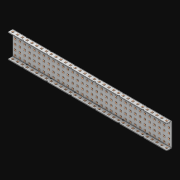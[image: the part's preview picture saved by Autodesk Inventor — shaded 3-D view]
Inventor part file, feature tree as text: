
AUTODESK INVENTOR PART (.ipt)
format: ipt  version: 2021 (Build 250183000, 183)  size: 3,894,272 bytes
history: native  units: in
note: dims shown in document units (in); Inventor stores cm internally (conversion verified against a paired STEP export)
features: extrude x232, other x231, sketch x4, thicken_offset x3, pattern_linear x3, imported_body x1
ambient origin geometry x8: Origin, YZ Plane, XZ Plane, XY Plane, X Axis, Y Axis, Z Axis, Center Point
bodies: Solid1 (feature_tree)
feature tree (474):
  thicken_offset  "Thicken1"
  thicken_offset  "Thicken2"
  thicken_offset  "Thicken3"
  pattern_linear  "Rectangular Pattern1"  Spacing1=0.001in  [1 undecoded]
  pattern_linear  "Rectangular Pattern2"  Spacing1=0.001in  [1 undecoded]
  pattern_linear  "Rectangular Pattern3"  Spacing1=0.182in  [1 undecoded]
  extrude  "Extrusion1"  Depth=0.063in TaperAngle=0.0deg
  sketch  "Sketch1"  dims[d0=0.001in]
  other  "Srf1"
  sketch  "Sketch2"  dims[d1=0.001in]
  other  "Srf2"
  sketch  "Sketch3"  dims[d2=0.001in]
  other  "Srf3"
  other  "Srf4"
  other  "Srf5"
  other  "Srf6"
  other  "Srf7"
  other  "Srf8"
  other  "Srf9"
  other  "Srf10"
  other  "Srf11"
  other  "Srf12"
  other  "Srf13"
  other  "Srf14"
  other  "Srf15"
  other  "Srf16"
  other  "Srf17"
  other  "Srf18"
  other  "Srf19"
  other  "Srf20"
  other  "Srf21"
  other  "Srf22"
  other  "Srf23"
  other  "Srf24"
  other  "Srf25"
  other  "Srf26"
  other  "Srf27"
  other  "Srf28"
  other  "Srf29"
  other  "Srf30"
  other  "Srf31"
  other  "Srf32"
  other  "Srf33"
  other  "Srf34"
  other  "Srf38"
  other  "Srf39"
  other  "Srf40"
  other  "Srf41"
  other  "Srf42"
  other  "Srf43"
  other  "Srf44"
  other  "Srf45"
  other  "Srf46"
  other  "Srf47"
  other  "Srf48"
  other  "Srf49"
  other  "Srf50"
  other  "Srf51"
  other  "Srf52"
  other  "Srf53"
  other  "Srf54"
  other  "Srf55"
  other  "Srf56"
  other  "Srf57"
  other  "Srf58"
  other  "Srf59"
  other  "Srf60"
  other  "Srf61"
  other  "Srf62"
  other  "Srf63"
  other  "Srf64"
  other  "Srf65"
  other  "Srf66"
  other  "Srf67"
  other  "Srf68"
  other  "Srf72"
  other  "Srf73"
  other  "Srf74"
  other  "Srf75"
  other  "Srf76"
  other  "Srf77"
  other  "Srf78"
  other  "Srf79"
  other  "Srf80"
  other  "Srf81"
  other  "Srf82"
  other  "Srf83"
  other  "Srf84"
  other  "Srf85"
  other  "Srf86"
  other  "Srf87"
  other  "Srf88"
  other  "Srf89"
  other  "Srf90"
  other  "Srf91"
  other  "Srf92"
  other  "Srf93"
  other  "Srf94"
  other  "Srf95"
  other  "Srf96"
  other  "Srf97"
  other  "Srf98"
  other  "Srf99"
  other  "Srf100"
  other  "Srf101"
  other  "Srf102"
  other  "Srf106"
  other  "Srf107"
  other  "Srf108"
  other  "Srf109"
  other  "Srf110"
  other  "Srf111"
  other  "Srf112"
  other  "Srf113"
  other  "Srf114"
  other  "Srf115"
  other  "Srf116"
  other  "Srf117"
  other  "Srf118"
  other  "Srf119"
  other  "Srf120"
  other  "Srf121"
  other  "Srf122"
  other  "Srf123"
  other  "Srf124"
  other  "Srf125"
  other  "Srf126"
  other  "Srf127"
  other  "Srf128"
  other  "Srf129"
  other  "Srf130"
  other  "Srf131"
  other  "Srf132"
  other  "Srf133"
  other  "Srf134"
  other  "Srf135"
  other  "Srf136"
  other  "Srf137"
  other  "Srf141"
  other  "Srf142"
  other  "Srf143"
  other  "Srf144"
  other  "Srf145"
  other  "Srf146"
  other  "Srf147"
  other  "Srf148"
  other  "Srf149"
  other  "Srf150"
  other  "Srf151"
  other  "Srf152"
  other  "Srf153"
  other  "Srf154"
  other  "Srf155"
  other  "Srf156"
  other  "Srf157"
  other  "Srf158"
  other  "Srf159"
  other  "Srf160"
  other  "Srf161"
  other  "Srf162"
  other  "Srf163"
  other  "Srf164"
  other  "Srf165"
  other  "Srf166"
  other  "Srf167"
  other  "Srf168"
  other  "Srf169"
  other  "Srf170"
  other  "Srf171"
  other  "Srf172"
  other  "Srf176"
  other  "Srf177"
  other  "Srf178"
  other  "Srf179"
  other  "Srf180"
  other  "Srf181"
  other  "Srf182"
  other  "Srf183"
  other  "Srf184"
  other  "Srf185"
  other  "Srf186"
  other  "Srf187"
  other  "Srf188"
  other  "Srf189"
  other  "Srf190"
  other  "Srf191"
  other  "Srf192"
  other  "Srf193"
  other  "Srf194"
  other  "Srf195"
  other  "Srf196"
  other  "Srf197"
  other  "Srf198"
  other  "Srf199"
  other  "Srf200"
  other  "Srf201"
  other  "Srf202"
  other  "Srf203"
  other  "Srf204"
  other  "Srf205"
  other  "Srf206"
  other  "Srf207"
  other  "Srf211"
  other  "Srf212"
  other  "Srf213"
  other  "Srf214"
  other  "Srf215"
  other  "Srf216"
  other  "Srf217"
  other  "Srf218"
  other  "Srf219"
  other  "Srf220"
  other  "Srf221"
  other  "Srf222"
  other  "Srf223"
  other  "Srf224"
  other  "Srf225"
  other  "Srf226"
  other  "Srf227"
  other  "Srf228"
  other  "Srf229"
  other  "Srf230"
  other  "Srf231"
  other  "Srf232"
  other  "Srf233"
  other  "Srf234"
  other  "Srf235"
  other  "Srf236"
  other  "Srf237"
  other  "Srf238"
  other  "Srf239"
  other  "Srf240"
  other  "Srf241"
  other  "Srf242"
  sketch  "Sketch4"  dims[d3=0.001in d4=0.001in d5=0.001in d6=0.182in d7=0.063in d8=0.0in d9=0.182in d10=0.063in d11=0.0in d12=0.182in d13=0.063in d14=0.0in d17=0.5in d18=12.9921in d20=0.5in d21=12.9921in d23=0.5in d24=1.9685in d26=0.5in d27=1.0in d28=0.0in]
  other  "Srf246"
  other  "Srf247"
  other  "Srf248"
  other  "Srf249"
  other  "Srf250"
  other  "Srf251"
  other  "Srf252"
  imported_body  "Imported1"
  extrude  "ExtrusionSrf1"  Depth=1.0in
  extrude  "ExtrusionSrf2"  Depth=0.063in TaperAngle=0.0deg
  extrude  "ExtrusionSrf3"  Depth=1.0in
  extrude  "ExtrusionSrf4"  Depth=0.063in TaperAngle=0.0deg
  extrude  "ExtrusionSrf5"  Depth=0.5in
  extrude  "ExtrusionSrf6"  Depth=1.0in
  extrude  "ExtrusionSrf7"  Depth=0.5in
  extrude  "ExtrusionSrf8"  Depth=1.0in
  extrude  "ExtrusionSrf9"  Depth=0.5in
  extrude  "ExtrusionSrf10"  Depth=0.5in
  extrude  "ExtrusionSrf11"  Depth=1.0in
  extrude  "ExtrusionSrf12"  TaperAngle=0.0deg  [1 undecoded]
  extrude  "ExtrusionSrf13"  [1 undecoded]
  extrude  "ExtrusionSrf14"  [1 undecoded]
  extrude  "ExtrusionSrf15"  [1 undecoded]
  extrude  "ExtrusionSrf16"  [1 undecoded]
  extrude  "ExtrusionSrf17"  [1 undecoded]
  extrude  "ExtrusionSrf18"  [1 undecoded]
  extrude  "ExtrusionSrf19"  [1 undecoded]
  extrude  "ExtrusionSrf20"  [1 undecoded]
  extrude  "ExtrusionSrf21"  [1 undecoded]
  extrude  "ExtrusionSrf22"  [1 undecoded]
  extrude  "ExtrusionSrf23"  [1 undecoded]
  extrude  "ExtrusionSrf24"  [1 undecoded]
  extrude  "ExtrusionSrf25"  [1 undecoded]
  extrude  "ExtrusionSrf26"  [1 undecoded]
  extrude  "ExtrusionSrf27"  [1 undecoded]
  extrude  "ExtrusionSrf28"  [1 undecoded]
  extrude  "ExtrusionSrf29"  [1 undecoded]
  extrude  "ExtrusionSrf30"  [1 undecoded]
  extrude  "ExtrusionSrf31"  [1 undecoded]
  extrude  "ExtrusionSrf32"  [1 undecoded]
  extrude  "ExtrusionSrf33"  [1 undecoded]
  extrude  "ExtrusionSrf34"  [1 undecoded]
  extrude  "ExtrusionSrf38"  [1 undecoded]
  extrude  "ExtrusionSrf39"  [1 undecoded]
  extrude  "ExtrusionSrf40"  [1 undecoded]
  extrude  "ExtrusionSrf41"  [1 undecoded]
  extrude  "ExtrusionSrf42"  [1 undecoded]
  extrude  "ExtrusionSrf43"  [1 undecoded]
  extrude  "ExtrusionSrf44"  [1 undecoded]
  extrude  "ExtrusionSrf45"  [1 undecoded]
  extrude  "ExtrusionSrf46"  [1 undecoded]
  extrude  "ExtrusionSrf47"  [1 undecoded]
  extrude  "ExtrusionSrf48"  [1 undecoded]
  extrude  "ExtrusionSrf49"  [1 undecoded]
  extrude  "ExtrusionSrf50"  [1 undecoded]
  extrude  "ExtrusionSrf51"  [1 undecoded]
  extrude  "ExtrusionSrf52"  [1 undecoded]
  extrude  "ExtrusionSrf53"  [1 undecoded]
  extrude  "ExtrusionSrf54"  [1 undecoded]
  extrude  "ExtrusionSrf55"  [1 undecoded]
  extrude  "ExtrusionSrf56"  [1 undecoded]
  extrude  "ExtrusionSrf57"  [1 undecoded]
  extrude  "ExtrusionSrf58"  [1 undecoded]
  extrude  "ExtrusionSrf59"  [1 undecoded]
  extrude  "ExtrusionSrf60"  [1 undecoded]
  extrude  "ExtrusionSrf61"  [1 undecoded]
  extrude  "ExtrusionSrf62"  [1 undecoded]
  extrude  "ExtrusionSrf63"  [1 undecoded]
  extrude  "ExtrusionSrf64"  [1 undecoded]
  extrude  "ExtrusionSrf65"  [1 undecoded]
  extrude  "ExtrusionSrf66"  [1 undecoded]
  extrude  "ExtrusionSrf67"  [1 undecoded]
  extrude  "ExtrusionSrf68"  [1 undecoded]
  extrude  "ExtrusionSrf72"  [1 undecoded]
  extrude  "ExtrusionSrf73"  [1 undecoded]
  extrude  "ExtrusionSrf74"  [1 undecoded]
  extrude  "ExtrusionSrf75"  [1 undecoded]
  extrude  "ExtrusionSrf76"  [1 undecoded]
  extrude  "ExtrusionSrf77"  [1 undecoded]
  extrude  "ExtrusionSrf78"  [1 undecoded]
  extrude  "ExtrusionSrf79"  [1 undecoded]
  extrude  "ExtrusionSrf80"  [1 undecoded]
  extrude  "ExtrusionSrf81"  [1 undecoded]
  extrude  "ExtrusionSrf82"  [1 undecoded]
  extrude  "ExtrusionSrf83"  [1 undecoded]
  extrude  "ExtrusionSrf84"  [1 undecoded]
  extrude  "ExtrusionSrf85"  [1 undecoded]
  extrude  "ExtrusionSrf86"  [1 undecoded]
  extrude  "ExtrusionSrf87"  [1 undecoded]
  extrude  "ExtrusionSrf88"  [1 undecoded]
  extrude  "ExtrusionSrf89"  [1 undecoded]
  extrude  "ExtrusionSrf90"  [1 undecoded]
  extrude  "ExtrusionSrf91"  [1 undecoded]
  extrude  "ExtrusionSrf92"  [1 undecoded]
  extrude  "ExtrusionSrf93"  [1 undecoded]
  extrude  "ExtrusionSrf94"  [1 undecoded]
  extrude  "ExtrusionSrf95"  [1 undecoded]
  extrude  "ExtrusionSrf96"  [1 undecoded]
  extrude  "ExtrusionSrf97"  [1 undecoded]
  extrude  "ExtrusionSrf98"  [1 undecoded]
  extrude  "ExtrusionSrf99"  [1 undecoded]
  extrude  "ExtrusionSrf100"  [1 undecoded]
  extrude  "ExtrusionSrf101"  [1 undecoded]
  extrude  "ExtrusionSrf102"  [1 undecoded]
  extrude  "ExtrusionSrf106"  [1 undecoded]
  extrude  "ExtrusionSrf107"  [1 undecoded]
  extrude  "ExtrusionSrf108"  [1 undecoded]
  extrude  "ExtrusionSrf109"  [1 undecoded]
  extrude  "ExtrusionSrf110"  [1 undecoded]
  extrude  "ExtrusionSrf111"  [1 undecoded]
  extrude  "ExtrusionSrf112"  [1 undecoded]
  extrude  "ExtrusionSrf113"  [1 undecoded]
  extrude  "ExtrusionSrf114"  [1 undecoded]
  extrude  "ExtrusionSrf115"  [1 undecoded]
  extrude  "ExtrusionSrf116"  [1 undecoded]
  extrude  "ExtrusionSrf117"  [1 undecoded]
  extrude  "ExtrusionSrf118"  [1 undecoded]
  extrude  "ExtrusionSrf119"  [1 undecoded]
  extrude  "ExtrusionSrf120"  [1 undecoded]
  extrude  "ExtrusionSrf121"  [1 undecoded]
  extrude  "ExtrusionSrf122"  [1 undecoded]
  extrude  "ExtrusionSrf123"  [1 undecoded]
  extrude  "ExtrusionSrf124"  [1 undecoded]
  extrude  "ExtrusionSrf125"  [1 undecoded]
  extrude  "ExtrusionSrf126"  [1 undecoded]
  extrude  "ExtrusionSrf127"  [1 undecoded]
  extrude  "ExtrusionSrf128"  [1 undecoded]
  extrude  "ExtrusionSrf129"  [1 undecoded]
  extrude  "ExtrusionSrf130"  [1 undecoded]
  extrude  "ExtrusionSrf131"  [1 undecoded]
  extrude  "ExtrusionSrf132"  [1 undecoded]
  extrude  "ExtrusionSrf133"  [1 undecoded]
  extrude  "ExtrusionSrf134"  [1 undecoded]
  extrude  "ExtrusionSrf135"  [1 undecoded]
  extrude  "ExtrusionSrf136"  [1 undecoded]
  extrude  "ExtrusionSrf137"  [1 undecoded]
  extrude  "ExtrusionSrf141"  [1 undecoded]
  extrude  "ExtrusionSrf142"  [1 undecoded]
  extrude  "ExtrusionSrf143"  [1 undecoded]
  extrude  "ExtrusionSrf144"  [1 undecoded]
  extrude  "ExtrusionSrf145"  [1 undecoded]
  extrude  "ExtrusionSrf146"  [1 undecoded]
  extrude  "ExtrusionSrf147"  [1 undecoded]
  extrude  "ExtrusionSrf148"  [1 undecoded]
  extrude  "ExtrusionSrf149"  [1 undecoded]
  extrude  "ExtrusionSrf150"  [1 undecoded]
  extrude  "ExtrusionSrf151"  [1 undecoded]
  extrude  "ExtrusionSrf152"  [1 undecoded]
  extrude  "ExtrusionSrf153"  [1 undecoded]
  extrude  "ExtrusionSrf154"  [1 undecoded]
  extrude  "ExtrusionSrf155"  [1 undecoded]
  extrude  "ExtrusionSrf156"  [1 undecoded]
  extrude  "ExtrusionSrf157"  [1 undecoded]
  extrude  "ExtrusionSrf158"  [1 undecoded]
  extrude  "ExtrusionSrf159"  [1 undecoded]
  extrude  "ExtrusionSrf160"  [1 undecoded]
  extrude  "ExtrusionSrf161"  [1 undecoded]
  extrude  "ExtrusionSrf162"  [1 undecoded]
  extrude  "ExtrusionSrf163"  [1 undecoded]
  extrude  "ExtrusionSrf164"  [1 undecoded]
  extrude  "ExtrusionSrf165"  [1 undecoded]
  extrude  "ExtrusionSrf166"  [1 undecoded]
  extrude  "ExtrusionSrf167"  [1 undecoded]
  extrude  "ExtrusionSrf168"  [1 undecoded]
  extrude  "ExtrusionSrf169"  [1 undecoded]
  extrude  "ExtrusionSrf170"  [1 undecoded]
  extrude  "ExtrusionSrf171"  [1 undecoded]
  extrude  "ExtrusionSrf172"  [1 undecoded]
  extrude  "ExtrusionSrf176"  [1 undecoded]
  extrude  "ExtrusionSrf177"  [1 undecoded]
  extrude  "ExtrusionSrf178"  [1 undecoded]
  extrude  "ExtrusionSrf179"  [1 undecoded]
  extrude  "ExtrusionSrf180"  [1 undecoded]
  extrude  "ExtrusionSrf181"  [1 undecoded]
  extrude  "ExtrusionSrf182"  [1 undecoded]
  extrude  "ExtrusionSrf183"  [1 undecoded]
  extrude  "ExtrusionSrf184"  [1 undecoded]
  extrude  "ExtrusionSrf185"  [1 undecoded]
  extrude  "ExtrusionSrf186"  [1 undecoded]
  extrude  "ExtrusionSrf187"  [1 undecoded]
  extrude  "ExtrusionSrf188"  [1 undecoded]
  extrude  "ExtrusionSrf189"  [1 undecoded]
  extrude  "ExtrusionSrf190"  [1 undecoded]
  extrude  "ExtrusionSrf191"  [1 undecoded]
  extrude  "ExtrusionSrf192"  [1 undecoded]
  extrude  "ExtrusionSrf193"  [1 undecoded]
  extrude  "ExtrusionSrf194"  [1 undecoded]
  extrude  "ExtrusionSrf195"  [1 undecoded]
  extrude  "ExtrusionSrf196"  [1 undecoded]
  extrude  "ExtrusionSrf197"  [1 undecoded]
  extrude  "ExtrusionSrf198"  [1 undecoded]
  extrude  "ExtrusionSrf199"  [1 undecoded]
  extrude  "ExtrusionSrf200"  [1 undecoded]
  extrude  "ExtrusionSrf201"  [1 undecoded]
  extrude  "ExtrusionSrf202"  [1 undecoded]
  extrude  "ExtrusionSrf203"  [1 undecoded]
  extrude  "ExtrusionSrf204"  [1 undecoded]
  extrude  "ExtrusionSrf205"  [1 undecoded]
  extrude  "ExtrusionSrf206"  [1 undecoded]
  extrude  "ExtrusionSrf207"  [1 undecoded]
  extrude  "ExtrusionSrf211"  [1 undecoded]
  extrude  "ExtrusionSrf212"  [1 undecoded]
  extrude  "ExtrusionSrf213"  [1 undecoded]
  extrude  "ExtrusionSrf214"  [1 undecoded]
  extrude  "ExtrusionSrf215"  [1 undecoded]
  extrude  "ExtrusionSrf216"  [1 undecoded]
  extrude  "ExtrusionSrf217"  [1 undecoded]
  extrude  "ExtrusionSrf218"  [1 undecoded]
  extrude  "ExtrusionSrf219"  [1 undecoded]
  extrude  "ExtrusionSrf220"  [1 undecoded]
  extrude  "ExtrusionSrf221"  [1 undecoded]
  extrude  "ExtrusionSrf222"  [1 undecoded]
  extrude  "ExtrusionSrf223"  [1 undecoded]
  extrude  "ExtrusionSrf224"  [1 undecoded]
  extrude  "ExtrusionSrf225"  [1 undecoded]
  extrude  "ExtrusionSrf226"  [1 undecoded]
  extrude  "ExtrusionSrf227"  [1 undecoded]
  extrude  "ExtrusionSrf228"  [1 undecoded]
  extrude  "ExtrusionSrf229"  [1 undecoded]
  extrude  "ExtrusionSrf230"  [1 undecoded]
  extrude  "ExtrusionSrf231"  [1 undecoded]
  extrude  "ExtrusionSrf232"  [1 undecoded]
  extrude  "ExtrusionSrf233"  [1 undecoded]
  extrude  "ExtrusionSrf234"  [1 undecoded]
  extrude  "ExtrusionSrf235"  [1 undecoded]
  extrude  "ExtrusionSrf236"  [1 undecoded]
  extrude  "ExtrusionSrf237"  [1 undecoded]
  extrude  "ExtrusionSrf238"  [1 undecoded]
  extrude  "ExtrusionSrf239"  [1 undecoded]
  extrude  "ExtrusionSrf240"  [1 undecoded]
  extrude  "ExtrusionSrf241"  [1 undecoded]
  extrude  "ExtrusionSrf242"  [1 undecoded]
  extrude  "ExtrusionSrf246"  [1 undecoded]
  extrude  "ExtrusionSrf247"  [1 undecoded]
  extrude  "ExtrusionSrf248"  [1 undecoded]
  extrude  "ExtrusionSrf249"  [1 undecoded]
  extrude  "ExtrusionSrf250"  [1 undecoded]
  extrude  "ExtrusionSrf251"  [1 undecoded]
  extrude  "ExtrusionSrf252"  [1 undecoded]
note: 223 required parameter values undecoded (feature->parameter linkage not recoverable at this tier; creation-order binding heuristic only, values carry confidence <= 0.55)
